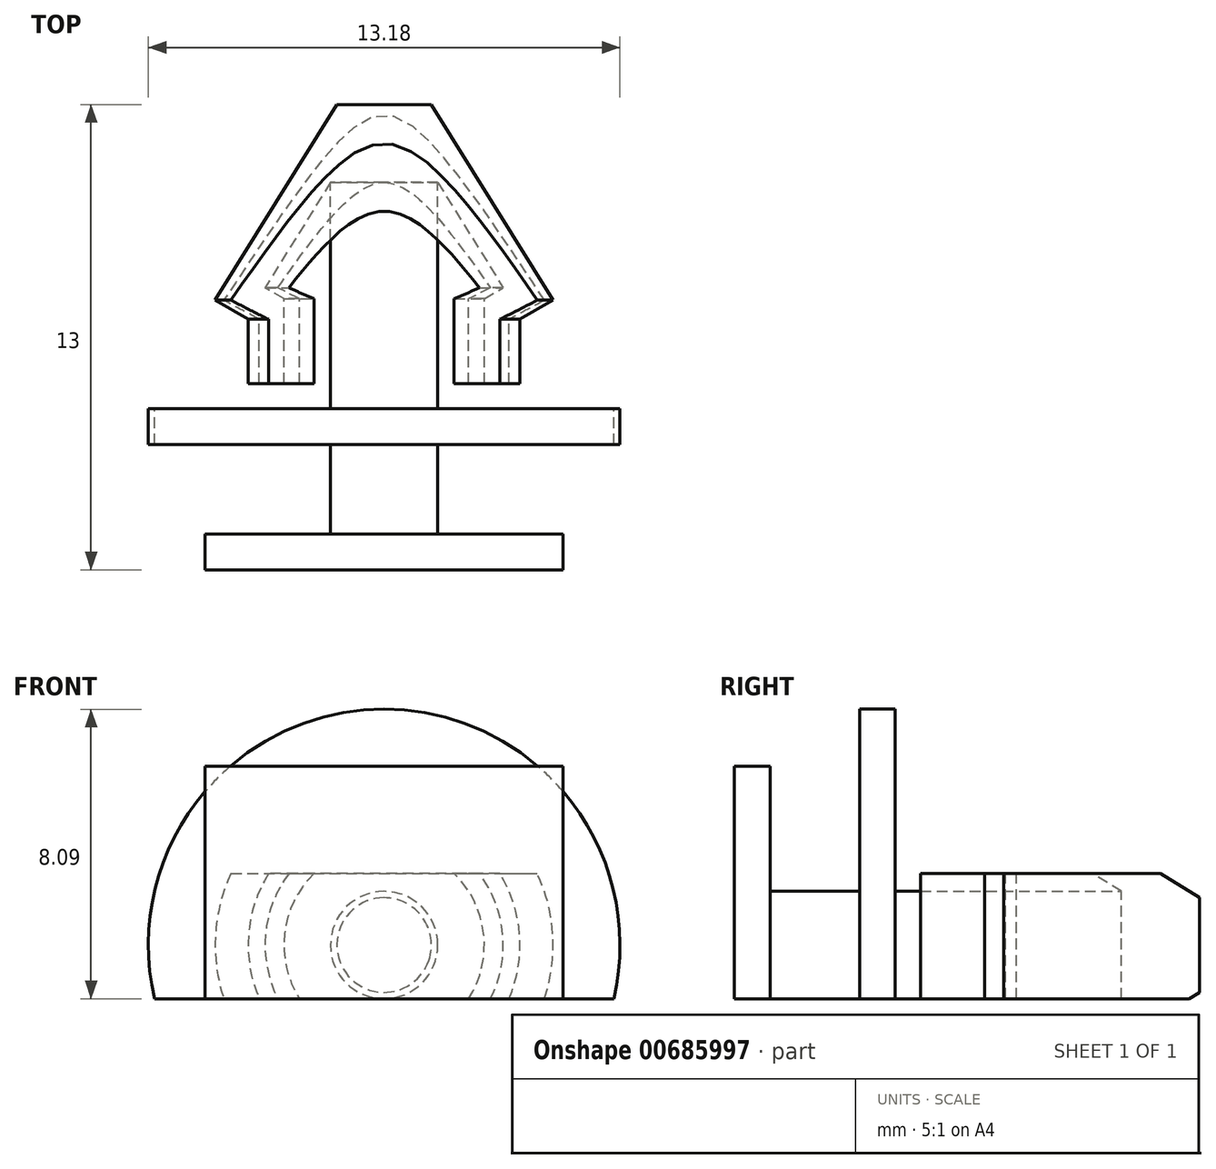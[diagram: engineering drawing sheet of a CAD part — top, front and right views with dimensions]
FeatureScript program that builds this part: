
annotation { "Feature Type Name" : "Feature", "Feature Type Description" : "" }
export const myFeature = defineFeature(function(context is Context, id is Id, definition is map)
    precondition{}
    {
        {
            var Q0;
            Q0=qCreatedBy(makeId("Top.planeOp"),FACE);
            var sketch = newSketch(context, id + "F0", { "sketchPlane" : qUnion([Q0])});
            skLineSegment(sketch, "E0.bottom", {"start": v(0, -6) * mm, "end": v(1.5, -6) * mm});
            skLineSegment(sketch, "E1", {"start": v(1.5, -6) * mm, "end": v(1.5, -3.5) * mm});
            skLineSegment(sketch, "E2", {"start": v(2.8, -1.8) * mm, "end": v(2.8, 0.58) * mm});
            skLineSegment(sketch, "E3", {"start": v(2.8, 0.58) * mm, "end": v(3.33, 0.88) * mm});
            skLineSegment(sketch, "E4", {"start": v(3.33, 0.88) * mm, "end": v(1.5, 3.82) * mm});
            skLineSegment(sketch, "E5", {"start": v(0, 6) * mm, "end": v(1.32, 6) * mm});
            skLineSegment(sketch, "E6", {"start": v(1.32, 6) * mm, "end": v(4.72, 0.53) * mm});
            skLineSegment(sketch, "E7", {"start": v(3.8, 0) * mm, "end": v(3.8, -1.8) * mm});
            skLineSegment(sketch, "E8", {"start": v(3.8, -1.8) * mm, "end": v(2.8, -1.8) * mm});
            skLineSegment(sketch, "E9", {"start": v(3.8, 0) * mm, "end": v(4.72, 0.53) * mm});
            skLineSegment(sketch, "E10", {"start": v(0, 6) * mm, "end": v(0, -6) * mm});
            skLineSegment(sketch, "E11", {"start": v(1.5, -3.5) * mm, "end": v(6.6, -3.5) * mm});
            skLineSegment(sketch, "E12", {"start": v(6.6, -3.5) * mm, "end": v(6.6, -2.5) * mm});
            skLineSegment(sketch, "E13", {"start": v(6.6, -2.5) * mm, "end": v(1.5, -2.5) * mm});
            skLineSegment(sketch, "E14.trimOffspring", {"start": v(1.5, -2.5) * mm, "end": v(1.5, 3.82) * mm});
            skSolve(sketch);
        }
        {
            var Q0;
            Q0=makeQuery(id+"F0.imprint","IMPRINT",FACE,{"disambiguationData":[TD([[makeQuery(id+"F0.imprint","IMPRINT",EDGE,{"derivedFrom":sQuery(id+"F0.wireOp",EDGE,"E0.bottom")}),1.0]])]});
            var Q1;
            Q1=sQuery(id+"F0.wireOp",EDGE,"E10");
            revolve(context, id + "F1", {"entities" : qUnion([Q0]), "axis" : qUnion([Q1]), "revolveType" : RevolveType.FULL});
        }
        {
            var Q0;
            Q0=makeQuery(id+"F1.opRevolve","SWEPT_FACE",FACE,{"disambiguationData":[OSD([sQuery(id+"F0.wireOp",EDGE,"E8")])]});
            var sketch = newSketch(context, id + "F2", { "sketchPlane" : qUnion([Q0])});
            skLineSegment(sketch, "E15.bottom", {"start": v(8, 2) * mm, "end": v(-8, 2) * mm});
            skLineSegment(sketch, "E15.top", {"start": v(8, 10) * mm, "end": v(-8, 10) * mm});
            skLineSegment(sketch, "E15.left", {"start": v(8, 2) * mm, "end": v(8, 10) * mm});
            skLineSegment(sketch, "E15.right", {"start": v(-8, 2) * mm, "end": v(-8, 10) * mm});
            skLineSegment(sketch, "E16.bottom", {"start": v(-8, -1.5) * mm, "end": v(8, -1.5) * mm});
            skLineSegment(sketch, "E16.top", {"start": v(-8, -9.5) * mm, "end": v(8, -9.5) * mm});
            skLineSegment(sketch, "E16.left", {"start": v(-8, -1.5) * mm, "end": v(-8, -9.5) * mm});
            skLineSegment(sketch, "E16.right", {"start": v(8, -1.5) * mm, "end": v(8, -9.5) * mm});
            skSolve(sketch);
        }
        {
            var Q0;
            Q0 = qSketchRegion(id + "F2", true);
            extrude(context, id + "F3", {"entities" : qUnion([Q0]), "operationType" : NewBodyOperationType.REMOVE, "oppositeDirection" : true, "depth" : 25 * mm, "offsetDistance" : 25 * mm});
        }
        {
            var Q0;
            Q0=qCreatedBy(makeId("Top.planeOp"),FACE);
            var sketch = newSketch(context, id + "F4", { "sketchPlane" : qUnion([Q0])});
            skLineSegment(sketch, "E17.bottom", {"start": v(-5, -6) * mm, "end": v(5, -6) * mm});
            skLineSegment(sketch, "E17.top", {"start": v(-5, -7) * mm, "end": v(5, -7) * mm});
            skLineSegment(sketch, "E17.left", {"start": v(-5, -6) * mm, "end": v(-5, -7) * mm});
            skLineSegment(sketch, "E17.right", {"start": v(5, -6) * mm, "end": v(5, -7) * mm});
            skSolve(sketch);
        }
        {
            var Q0;
            Q0 = qSketchRegion(id + "F4", true);
            extrude(context, id + "F5", {"entities" : qUnion([Q0]), "operationType" : NewBodyOperationType.ADD, "depth" : 5 * mm, "offsetDistance" : 25 * mm, "hasSecondDirection" : true, "secondDirectionOppositeDirection" : true, "secondDirectionDepth" : 1.5 * mm});
        }
        {
            var Q0;
            Q0=makeQuery(id+"F1.opRevolve","SWEPT_FACE",FACE,{"disambiguationData":[OSD([sQuery(id+"F0.wireOp",EDGE,"E13")])]});
            var sketch = newSketch(context, id + "F6", { "sketchPlane" : qUnion([Q0])});
            skLineSegment(sketch, "E18", {"start": v(-6.42, -1.5) * mm, "end": v(6.42, -1.5) * mm});
            skSolve(sketch);
        }
        {
            var Q0;
            Q0 = qSketchRegion(id + "F6", true);
            var Q1;
            {var subQ0=sQuery(id+"F6.wireOp",EDGE,"E18");var subQ1=sQuery(id+"F0.wireOp",EDGE,"E13");var subQ2=makeQuery(id+"F1.opRevolve","SWEPT_EDGE",EDGE,{"disambiguationData":[OSD([sQuery(id+"F0.wireOp",EDGE,"E12"),subQ1])]});var subQ3=makeQuery(id+"F6.imprint","INTERSECT",VERTEX,{"disambiguationData":[OD(0.0)],"derivedFrom":[subQ2,subQ0]});Q1=makeQuery(id+"F6.imprint","IMPRINT",FACE,{"disambiguationData":[TD([[makeQuery(id+"F6.imprint","IMPRINT",EDGE,{"disambiguationData":[TD([[subQ3,-1.0]])],"derivedFrom":subQ0}),-1.0]])]});}
            extrude(context, id + "F7", {"entities" : qUnion([Q0, Q1]), "operationType" : NewBodyOperationType.REMOVE, "oppositeDirection" : true, "depth" : 10 * mm, "offsetDistance" : 25 * mm});
        }
    });
